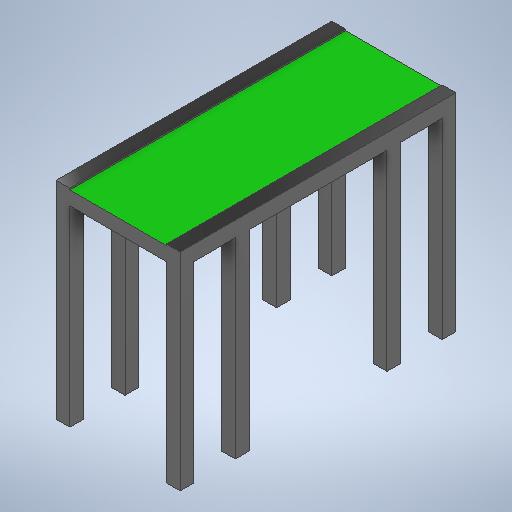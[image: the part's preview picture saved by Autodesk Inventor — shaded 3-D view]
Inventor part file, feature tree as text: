
AUTODESK INVENTOR PART (.ipt)
format: ipt  version: 2025.2 (Build 292293000, 293)  size: 326,144 bytes
history: native  units: mm
features: extrude x5, sketch x5
ambient origin geometry x8: Origin, YZ Plane, XZ Plane, XY Plane, X Axis, Y Axis, Z Axis, Center Point
bodies: Solid2 (feature_tree)
feature tree (10):
  extrude  "Extrusion6"  Depth=100.0mm
  extrude  "Extrusion7"  Depth=100.0mm TaperAngle=0.0deg
  extrude  "Extrusion9"  Depth=500.0mm
  extrude  "Extrusión11"  Depth=600.0mm
  extrude  "Extrusión12"  Depth=1500.0mm TaperAngle=0.0deg
  sketch  "Sketch9"  dims[d70=900.0mm d71=100.0mm]
  sketch  "Sketch10"  dims[d72=100.0mm d75=1790.0mm d76=0.0mm]
  sketch  "Sketch13"  dims[d83=500.0mm d84=500.0mm]
  sketch  "Boceto15"  dims[d85=600.0mm d86=600.0mm]
  sketch  "Boceto16"  dims[d87=900.0mm d88=0.0mm d96=290.0mm d97=0.0mm d106=2000.0mm d108=1500.0mm d109=0.0mm d110=500.0mm d111=500.0mm d112=100.0mm d113=100.0mm d114=100.0mm d115=100.0mm d116=1500.0mm d117=0.0mm d53=0.5mm d54=0.872665mm d55=0.5mm d56=0.872665mm d102=0.5mm d103=0.872665mm d104=0.5mm d105=0.872665mm]
